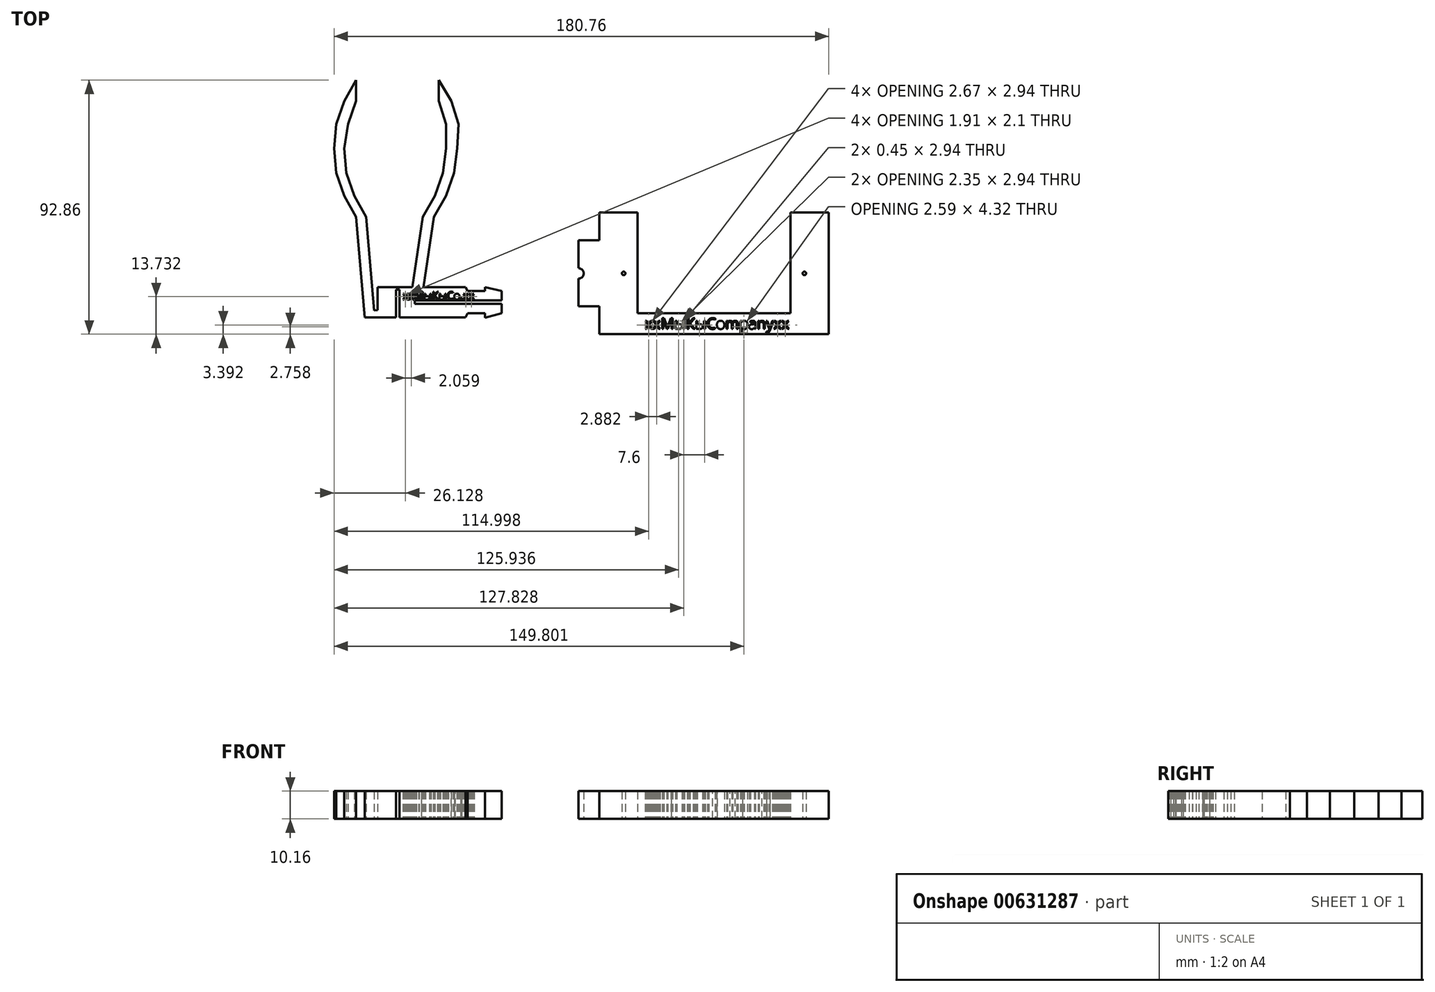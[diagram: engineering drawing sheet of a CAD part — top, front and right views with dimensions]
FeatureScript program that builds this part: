
annotation { "Feature Type Name" : "Feature", "Feature Type Description" : "" }
export const myFeature = defineFeature(function(context is Context, id is Id, definition is map)
    precondition{}
    {
        {
            var Q0;
            Q0=qCreatedBy(makeId("Top.planeOp"),FACE);
            var sketch = newSketch(context, id + "F0", { "sketchPlane" : qUnion([Q0])});
            skLineSegment(sketch, "E0", {"start": v(0, 0) * mm, "end": v(-6.14, -1.64) * mm});
            skLineSegment(sketch, "E1", {"start": v(-6.14, -1.64) * mm, "end": v(-6.14, 0) * mm});
            skLineSegment(sketch, "E2", {"start": v(-6.14, 0) * mm, "end": v(-12.49, 0) * mm});
            skLineSegment(sketch, "E3", {"start": v(-12.49, 0) * mm, "end": v(-13.29, -1.42) * mm});
            skLineSegment(sketch, "E4", {"start": v(-13.29, -1.42) * mm, "end": v(-37.42, -1.42) * mm});
            skLineSegment(sketch, "E5", {"start": v(-37.42, -1.42) * mm, "end": v(-37.42, 8.74) * mm});
            skLineSegment(sketch, "E6", {"start": v(-37.42, 8.74) * mm, "end": v(-38.69, 8.74) * mm});
            skLineSegment(sketch, "E7", {"start": v(-38.69, 8.74) * mm, "end": v(-38.69, -1.42) * mm});
            skLineSegment(sketch, "E8", {"start": v(-38.69, -1.42) * mm, "end": v(-50.12, -1.42) * mm});
            skLineSegment(sketch, "E9", {"start": v(-50.12, -1.42) * mm, "end": v(-53.2, 35.29) * mm});
            skLineSegment(sketch, "E10", {"start": v(-53.2, 35.29) * mm, "end": v(-57.6, 43) * mm});
            skLineSegment(sketch, "E11", {"start": v(-57.6, 43) * mm, "end": v(-60.53, 51.4) * mm});
            skLineSegment(sketch, "E12", {"start": v(-60.53, 51.4) * mm, "end": v(-61.28, 60.26) * mm});
            skLineSegment(sketch, "E13", {"start": v(-61.28, 60.26) * mm, "end": v(-60.53, 69.12) * mm});
            skLineSegment(sketch, "E14", {"start": v(-60.53, 69.12) * mm, "end": v(-57.6, 77.51) * mm});
            skLineSegment(sketch, "E15", {"start": v(-57.6, 77.51) * mm, "end": v(-53.2, 85.24) * mm});
            skLineSegment(sketch, "E16", {"start": v(-53.2, 85.24) * mm, "end": v(-53.2, 77.62) * mm});
            skLineSegment(sketch, "E17", {"start": v(-53.2, 77.62) * mm, "end": v(-56.17, 69.12) * mm});
            skLineSegment(sketch, "E18", {"start": v(-56.17, 69.12) * mm, "end": v(-57.6, 60.26) * mm});
            skLineSegment(sketch, "E19", {"start": v(-57.6, 60.26) * mm, "end": v(-56.86, 51.4) * mm});
            skLineSegment(sketch, "E20", {"start": v(-56.86, 51.4) * mm, "end": v(-53.92, 43) * mm});
            skLineSegment(sketch, "E21", {"start": v(-53.92, 43) * mm, "end": v(-49.52, 35.29) * mm});
            skLineSegment(sketch, "E22", {"start": v(-49.52, 35.29) * mm, "end": v(-46.65, 1.12) * mm});
            skLineSegment(sketch, "E23", {"start": v(-46.65, 1.12) * mm, "end": v(-45.38, 1.22) * mm});
            skLineSegment(sketch, "E24", {"start": v(-45.38, 1.22) * mm, "end": v(-45.38, 9.6) * mm});
            skLineSegment(sketch, "E25", {"start": v(-45.38, 9.6) * mm, "end": v(-32.68, 9.6) * mm});
            skLineSegment(sketch, "E26", {"start": v(-32.68, 9.6) * mm, "end": v(-28.81, 35.29) * mm});
            skLineSegment(sketch, "E27", {"start": v(-37.42, -1.42) * mm, "end": v(-28.81, -1.42) * mm});
            skLineSegment(sketch, "E28", {"start": v(-28.81, -1.42) * mm, "end": v(-24.77, -1.42) * mm});
            skLineSegment(sketch, "E29", {"start": v(-28.81, -1.42) * mm, "end": v(-20.38, -1.42) * mm});
            skLineSegment(sketch, "E30", {"start": v(-28.81, -1.42) * mm, "end": v(-17.46, -1.42) * mm});
            skLineSegment(sketch, "E31", {"start": v(-20.38, 43.01) * mm, "end": v(-17.46, 51.4) * mm});
            skLineSegment(sketch, "E32", {"start": v(-28.81, -1.42) * mm, "end": v(-16.34, -1.42) * mm});
            skLineSegment(sketch, "E33", {"start": v(-17.46, 51.4) * mm, "end": v(-16.34, 60.23) * mm});
            skLineSegment(sketch, "E34", {"start": v(-16.34, 60.23) * mm, "end": v(-15.8, 69.12) * mm});
            skLineSegment(sketch, "E35", {"start": v(-15.8, 69.12) * mm, "end": v(-18.42, 77.62) * mm});
            skLineSegment(sketch, "E36", {"start": v(-18.42, 77.62) * mm, "end": v(-23, 85.24) * mm});
            skLineSegment(sketch, "E37", {"start": v(-23, 85.24) * mm, "end": v(-23, 77.62) * mm});
            skLineSegment(sketch, "E38", {"start": v(-23, 77.62) * mm, "end": v(-20.38, 69.12) * mm});
            skLineSegment(sketch, "E39", {"start": v(-20.38, 69.12) * mm, "end": v(-20.38, 60.23) * mm});
            skLineSegment(sketch, "E40", {"start": v(-20.38, 60.23) * mm, "end": v(-21.5, 51.4) * mm});
            skLineSegment(sketch, "E41", {"start": v(-21.5, 51.4) * mm, "end": v(-24.42, 43.01) * mm});
            skLineSegment(sketch, "E42", {"start": v(-24.42, 43.01) * mm, "end": v(-28.81, 35.29) * mm});
            skLineSegment(sketch, "E43", {"start": v(-20.38, 43.01) * mm, "end": v(-24.77, 35.29) * mm});
            skLineSegment(sketch, "E44", {"start": v(-24.77, 35.29) * mm, "end": v(-28.65, 9.6) * mm});
            skLineSegment(sketch, "E45", {"start": v(-28.65, 9.6) * mm, "end": v(-13.29, 9.6) * mm});
            skLineSegment(sketch, "E46", {"start": v(-13.29, 9.6) * mm, "end": v(-12.49, 8.19) * mm});
            skLineSegment(sketch, "E47", {"start": v(-12.49, 8.19) * mm, "end": v(-6.14, 8.19) * mm});
            skLineSegment(sketch, "E48", {"start": v(-6.14, 8.19) * mm, "end": v(-6.14, 9.6) * mm});
            skLineSegment(sketch, "E49", {"start": v(-6.14, 9.6) * mm, "end": v(0, 8.19) * mm});
            skLineSegment(sketch, "E50", {"start": v(-31.75, 4.14) * mm, "end": v(-31.75, 4.06) * mm});
            skLineSegment(sketch, "E51", {"start": v(0, 8.19) * mm, "end": v(0, 4.8) * mm});
            skLineSegment(sketch, "E52", {"start": v(0, 4.8) * mm, "end": v(-31.75, 4.8) * mm});
            skLineSegment(sketch, "E53", {"start": v(-31.75, 4.8) * mm, "end": v(-31.75, 3.53) * mm});
            skLineSegment(sketch, "E54", {"start": v(-31.75, 3.53) * mm, "end": v(0, 3.53) * mm});
            skLineSegment(sketch, "E55", {"start": v(0, 3.53) * mm, "end": v(0, 0) * mm});
            skText(sketch, "E56", { "text": "xxМыКыСo.xx", "fontName": "OpenSans-Regular.ttf"});
            const initialGuessF0  = {"E56": [-0.03618, 0.00506, 1, 0, 0.00283]};
            skSetInitialGuess(sketch, initialGuessF0);
            skSolve(sketch);
        }
        {
            var Q0;
            Q0=makeQuery(id+"F0.imprint","IMPRINT",FACE,{"disambiguationData":[TD([[makeQuery(id+"F0.imprint","IMPRINT",EDGE,{"derivedFrom":sQuery(id+"F0.wireOp",EDGE,"E0")}),-1.0]])]});
            extrude(context, id + "F1", {"entities" : qUnion([Q0]), "depth" : 10.16 * mm, "offsetDistance" : 25.4 * mm});
        }
        {
            var Q0;
            Q0=qCreatedBy(makeId("Top.planeOp"),FACE);
            var sketch = newSketch(context, id + "F2", { "sketchPlane" : qUnion([Q0])});
            skLineSegment(sketch, "E57", {"start": v(105.5, 0) * mm, "end": v(49.63, 0) * mm});
            skLineSegment(sketch, "E58", {"start": v(49.63, 0) * mm, "end": v(49.63, 29.2) * mm});
            skLineSegment(sketch, "E59", {"start": v(105.5, 0) * mm, "end": v(105.5, 29.2) * mm});
            skLineSegment(sketch, "E60", {"start": v(49.63, 29.2) * mm, "end": v(49.63, 36.83) * mm});
            skLineSegment(sketch, "E61", {"start": v(49.63, 36.83) * mm, "end": v(35.66, 36.83) * mm});
            skLineSegment(sketch, "E62", {"start": v(105.5, 29.2) * mm, "end": v(105.5, 36.83) * mm});
            skLineSegment(sketch, "E63", {"start": v(105.5, 36.83) * mm, "end": v(119.48, 36.83) * mm});
            skLineSegment(sketch, "E64", {"start": v(119.48, 36.83) * mm, "end": v(119.48, 0) * mm});
            skLineSegment(sketch, "E65", {"start": v(119.48, 0) * mm, "end": v(119.48, -7.62) * mm});
            skLineSegment(sketch, "E66", {"start": v(119.48, -7.62) * mm, "end": v(35.66, -7.62) * mm});
            skLineSegment(sketch, "E67", {"start": v(35.66, -7.62) * mm, "end": v(35.66, 2.54) * mm});
            skLineSegment(sketch, "E68", {"start": v(35.66, 2.54) * mm, "end": v(28.04, 2.54) * mm});
            skLineSegment(sketch, "E69", {"start": v(35.66, 36.83) * mm, "end": v(35.66, 26.67) * mm});
            skLineSegment(sketch, "E70", {"start": v(35.66, 26.67) * mm, "end": v(28.04, 26.67) * mm});
            skLineSegment(sketch, "E71", {"start": v(28.04, 26.67) * mm, "end": v(28.04, 16.5) * mm});
            skLineSegment(sketch, "E72", {"start": v(28.04, 2.54) * mm, "end": v(28.04, 12.7) * mm});
            skCircle(sketch, "E73", {"center": v(28.04, 14.6) * mm, "radius": 1.9 * mm});
            skLineSegment(sketch, "E74", {"start": v(49.63, 0) * mm, "end": v(49.63, 14.6) * mm});
            skLineSegment(sketch, "E75", {"start": v(49.63, 14.6) * mm, "end": v(44.55, 14.6) * mm});
            skCircle(sketch, "E76", {"center": v(44.55, 14.6) * mm, "radius": 0.64 * mm});
            skLineSegment(sketch, "E77", {"start": v(105.5, 14.6) * mm, "end": v(110.59, 14.6) * mm});
            skCircle(sketch, "E78", {"center": v(110.59, 14.6) * mm, "radius": 0.64 * mm});
            skText(sketch, "E79", { "text": "xxМыКыСompanyxx", "fontName": "OpenSans-Regular.ttf"});
            const initialGuessF2  = {"E79": [0.05228, -0.0057, 1, 0, 0.00396]};
            skSetInitialGuess(sketch, initialGuessF2);
            skSolve(sketch);
        }
        {
            var Q0;
            Q0=makeQuery(id+"F2.imprint","IMPRINT",FACE,{"disambiguationData":[TD([[makeQuery(id+"F2.imprint","IMPRINT",EDGE,{"derivedFrom":sQuery(id+"F2.wireOp",EDGE,"E57")}),1.0]])]});
            extrude(context, id + "F3", {"entities" : qUnion([Q0]), "depth" : 10.16 * mm, "offsetDistance" : 25.4 * mm});
        }
    });
